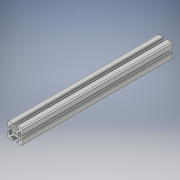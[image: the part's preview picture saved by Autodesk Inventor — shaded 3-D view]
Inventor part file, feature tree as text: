
AUTODESK INVENTOR PART (.ipt)
format: ipt  version: 2019 (Build 230136000, 136)  size: 222,208 bytes
history: native  units: mm
features: other x7, extrude x1, sketch x1
ambient origin geometry x8: Origin, YZ Plane, XZ Plane, XY Plane, X Axis, Y Axis, Z Axis, Center Point
bodies: Solid1 (feature_tree)
feature tree (9):
  extrude  "Extrusion1"  [1 undecoded]
  other  "to_parts_XY"
  other  "to_parts_YZ"
  other  "to_parts_ZX"
  other  "to_parts_X"
  other  "to_parts_Y"
  other  "to_parts_Z"
  other  "to_parts_Center"
  sketch  "Sketch_1"  dims[d0=400.0mm d1=0.0mm]
note: 1 required parameter value undecoded (feature->parameter linkage not recoverable at this tier; creation-order binding heuristic only, values carry confidence <= 0.55)
